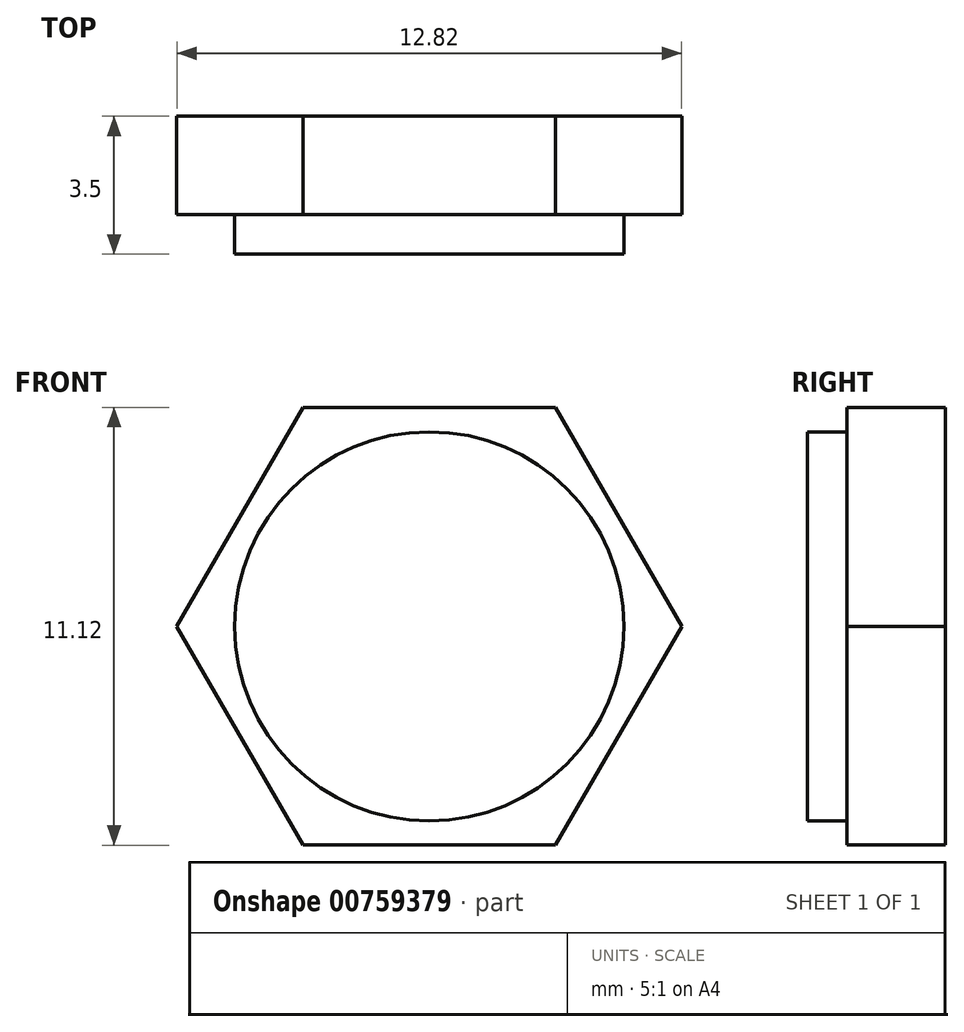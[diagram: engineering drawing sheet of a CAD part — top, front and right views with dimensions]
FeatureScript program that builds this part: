
annotation { "Feature Type Name" : "Feature", "Feature Type Description" : "" }
export const myFeature = defineFeature(function(context is Context, id is Id, definition is map)
    precondition{}
    {
        {
            var Q0;
            Q0=qCreatedBy(makeId("Front.planeOp"),FACE);
            var sketch = newSketch(context, id + "F0", { "sketchPlane" : qUnion([Q0])});
            skCircle(sketch, "E0.cCircle", {"center": v(0, 0) * mm, "radius": 5.56 * mm, "construction": true});
            skLineSegment(sketch, "E0.0", {"start": v(3.2, -5.56) * mm, "end": v(-3.2, -5.56) * mm});
            skLineSegment(sketch, "E0.1", {"start": v(-3.2, -5.56) * mm, "end": v(-6.41, 0) * mm});
            skLineSegment(sketch, "E0.2", {"start": v(-6.41, 0) * mm, "end": v(-3.2, 5.56) * mm});
            skLineSegment(sketch, "E0.3", {"start": v(-3.2, 5.56) * mm, "end": v(3.2, 5.56) * mm});
            skLineSegment(sketch, "E0.4", {"start": v(3.2, 5.56) * mm, "end": v(6.41, 0) * mm});
            skLineSegment(sketch, "E0.5", {"start": v(6.41, 0) * mm, "end": v(3.2, -5.56) * mm});
            skPoint(sketch, "E0.0.midPoint", {"position": v(0, -5.56) * mm});
            skCircle(sketch, "E1", {"center": v(0, 0) * mm, "radius": 5 * mm});
            skSolve(sketch);
        }
        {
            var Q0;
            Q0=makeQuery(id+"F0.imprint","IMPRINT",FACE,{"disambiguationData":[TD([[makeQuery(id+"F0.imprint","IMPRINT",EDGE,{"derivedFrom":sQuery(id+"F0.wireOp",EDGE,"E0.0")}),-1.0]])]});
            var Q1;
            Q1=makeQuery(id+"F0.imprint","IMPRINT",FACE,{"disambiguationData":[TD([[makeQuery(id+"F0.imprint","IMPRINT",EDGE,{"derivedFrom":sQuery(id+"F0.wireOp",EDGE,"E1")}),1.0]])]});
            extrude(context, id + "F1", {"entities" : qUnion([Q0, Q1]), "depth" : 2.5 * mm, "offsetDistance" : 25 * mm});
        }
        {
            var Q0;
            Q0=makeQuery(id+"F1.opExtrude","CAP_FACE",FACE,{"disambiguationData":[OSD([sQuery(id+"F0.wireOp",EDGE,"E0.0"),sQuery(id+"F0.wireOp",EDGE,"E0.1"),sQuery(id+"F0.wireOp",EDGE,"E0.2"),sQuery(id+"F0.wireOp",EDGE,"E0.3"),sQuery(id+"F0.wireOp",EDGE,"E0.4"),sQuery(id+"F0.wireOp",EDGE,"E0.5")])],"isStart":false});
            var sketch = newSketch(context, id + "F2", { "sketchPlane" : qUnion([Q0])});
            skCircle(sketch, "E2", {"center": v(0, 0) * mm, "radius": 4.94 * mm});
            skSolve(sketch);
        }
        {
            var Q0;
            Q0 = qSketchRegion(id + "F2", true);
            extrude(context, id + "F3", {"entities" : qUnion([Q0]), "operationType" : NewBodyOperationType.ADD, "depth" : 1 * mm, "offsetDistance" : 25 * mm});
        }
    });
